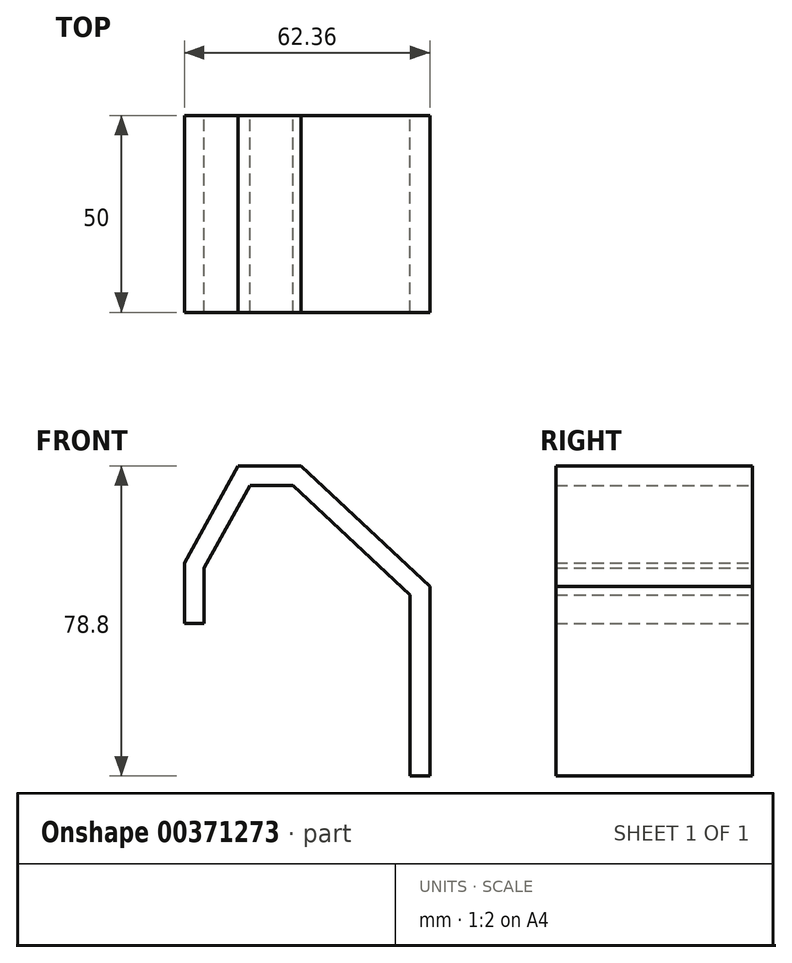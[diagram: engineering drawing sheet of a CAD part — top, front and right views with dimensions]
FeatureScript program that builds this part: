
annotation { "Feature Type Name" : "Feature", "Feature Type Description" : "" }
export const myFeature = defineFeature(function(context is Context, id is Id, definition is map)
    precondition{}
    {
        {
            var Q0;
            Q0=qCreatedBy(makeId("Front.planeOp"),FACE);
            var sketch = newSketch(context, id + "F0", { "sketchPlane" : qUnion([Q0])});
            skLineSegment(sketch, "E0", {"start": v(0, 0) * mm, "end": v(0, 46) * mm});
            skLineSegment(sketch, "E1", {"start": v(0, 46) * mm, "end": v(-49, 46) * mm, "construction": true});
            skLineSegment(sketch, "E2", {"start": v(0, 46) * mm, "end": v(-29.74, 73.8) * mm});
            skLineSegment(sketch, "E3", {"start": v(-29.74, 73.8) * mm, "end": v(-40.74, 73.8) * mm});
            skLineSegment(sketch, "E4", {"start": v(-40.74, 73.8) * mm, "end": v(-52.36, 52.8) * mm});
            skLineSegment(sketch, "E5", {"start": v(-52.36, 52.8) * mm, "end": v(-52.36, 38.8) * mm});
            skLineSegment(sketch, "E6.0", {"start": v(-57.36, 54.1) * mm, "end": v(-57.36, 38.8) * mm});
            skLineSegment(sketch, "E6.1", {"start": v(5, 0) * mm, "end": v(5, 48.17) * mm});
            skLineSegment(sketch, "E6.2", {"start": v(5, 48.17) * mm, "end": v(-27.77, 78.8) * mm});
            skLineSegment(sketch, "E6.3", {"start": v(-27.77, 78.8) * mm, "end": v(-43.7, 78.8) * mm});
            skLineSegment(sketch, "E6.4", {"start": v(-43.7, 78.8) * mm, "end": v(-57.36, 54.1) * mm});
            skLineSegment(sketch, "E7", {"start": v(-57.36, 38.8) * mm, "end": v(-52.36, 38.8) * mm});
            skLineSegment(sketch, "E8", {"start": v(0, 0) * mm, "end": v(5, 0) * mm});
            skSolve(sketch);
        }
        {
            var Q0;
            Q0=makeQuery(id+"F0.imprint","IMPRINT",FACE,{"disambiguationData":[TD([[makeQuery(id+"F0.imprint","IMPRINT",EDGE,{"derivedFrom":sQuery(id+"F0.wireOp",EDGE,"E0")}),-1.0]])]});
            extrude(context, id + "F1", {"entities" : qUnion([Q0]), "depth" : 50 * mm});
        }
    });
